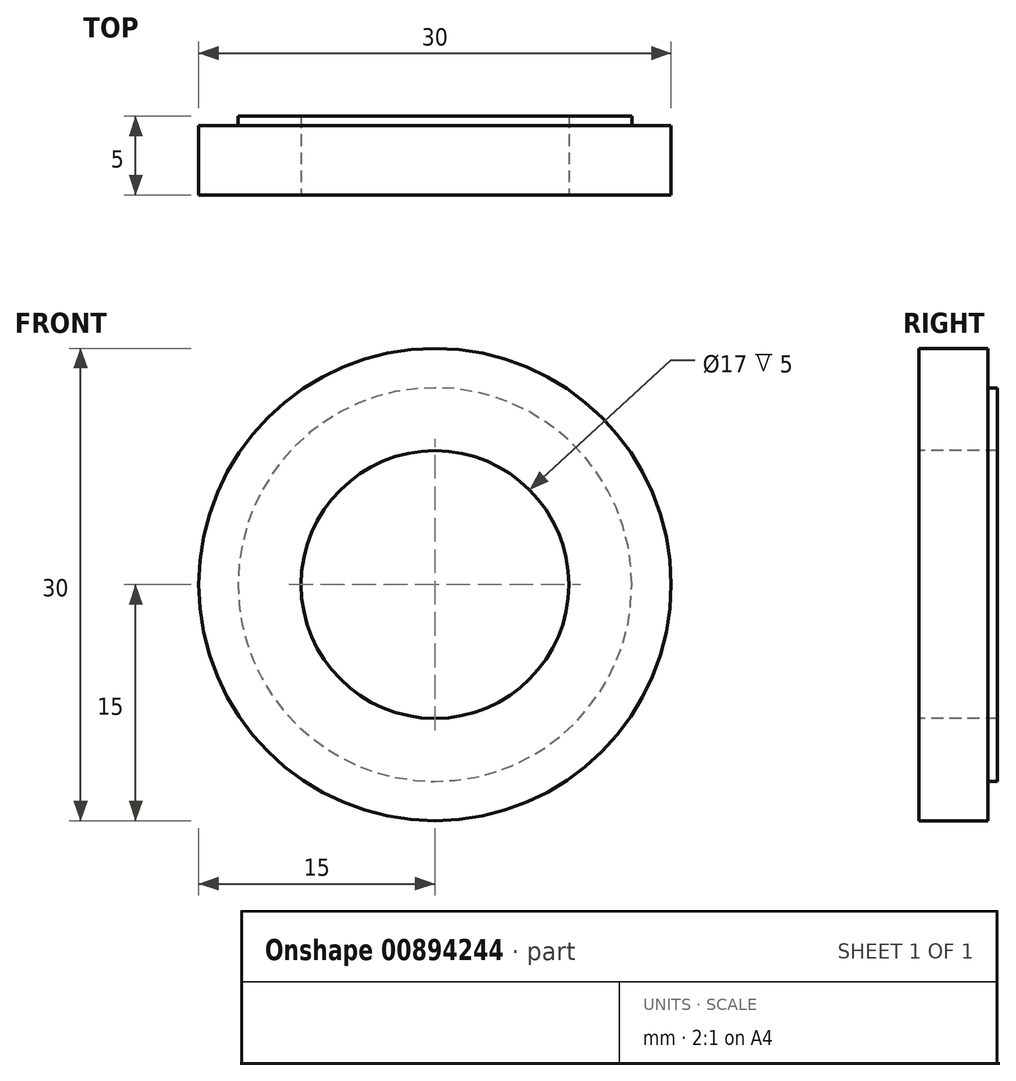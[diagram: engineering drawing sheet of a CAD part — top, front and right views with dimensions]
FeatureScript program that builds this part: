
annotation { "Feature Type Name" : "Feature", "Feature Type Description" : "" }
export const myFeature = defineFeature(function(context is Context, id is Id, definition is map)
    precondition{}
    {
        {
            var Q0;
            Q0=qCreatedBy(makeId("Right.planeOp"),FACE);
            var sketch = newSketch(context, id + "F0", { "sketchPlane" : qUnion([Q0])});
            skLineSegment(sketch, "E0", {"start": v(0, 0) * mm, "end": v(0, 8.5) * mm, "construction": true});
            skLineSegment(sketch, "E1", {"start": v(0, 8.5) * mm, "end": v(5, 8.5) * mm});
            skLineSegment(sketch, "E2", {"start": v(5, 8.5) * mm, "end": v(5, 12.5) * mm});
            skLineSegment(sketch, "E3", {"start": v(5, 12.5) * mm, "end": v(4.4, 12.5) * mm});
            skLineSegment(sketch, "E4", {"start": v(4.4, 12.5) * mm, "end": v(4.4, 15) * mm});
            skLineSegment(sketch, "E5", {"start": v(4.4, 15) * mm, "end": v(0, 15) * mm});
            skLineSegment(sketch, "E6", {"start": v(0, 15) * mm, "end": v(0, 8.5) * mm});
            skLineSegment(sketch, "E7", {"start": v(0, 0) * mm, "end": v(5, 0) * mm});
            skSolve(sketch);
        }
        {
            var Q0;
            Q0 = qSketchRegion(id + "F0", true);
            var Q1;
            Q1=sQuery(id+"F0.wireOp",EDGE,"E7");
            revolve(context, id + "F1", {"surfaceOperationType" : NewSurfaceOperationType.NEW, "entities" : qUnion([Q0]), "axis" : qUnion([Q1]), "revolveType" : RevolveType.FULL});
        }
    });
